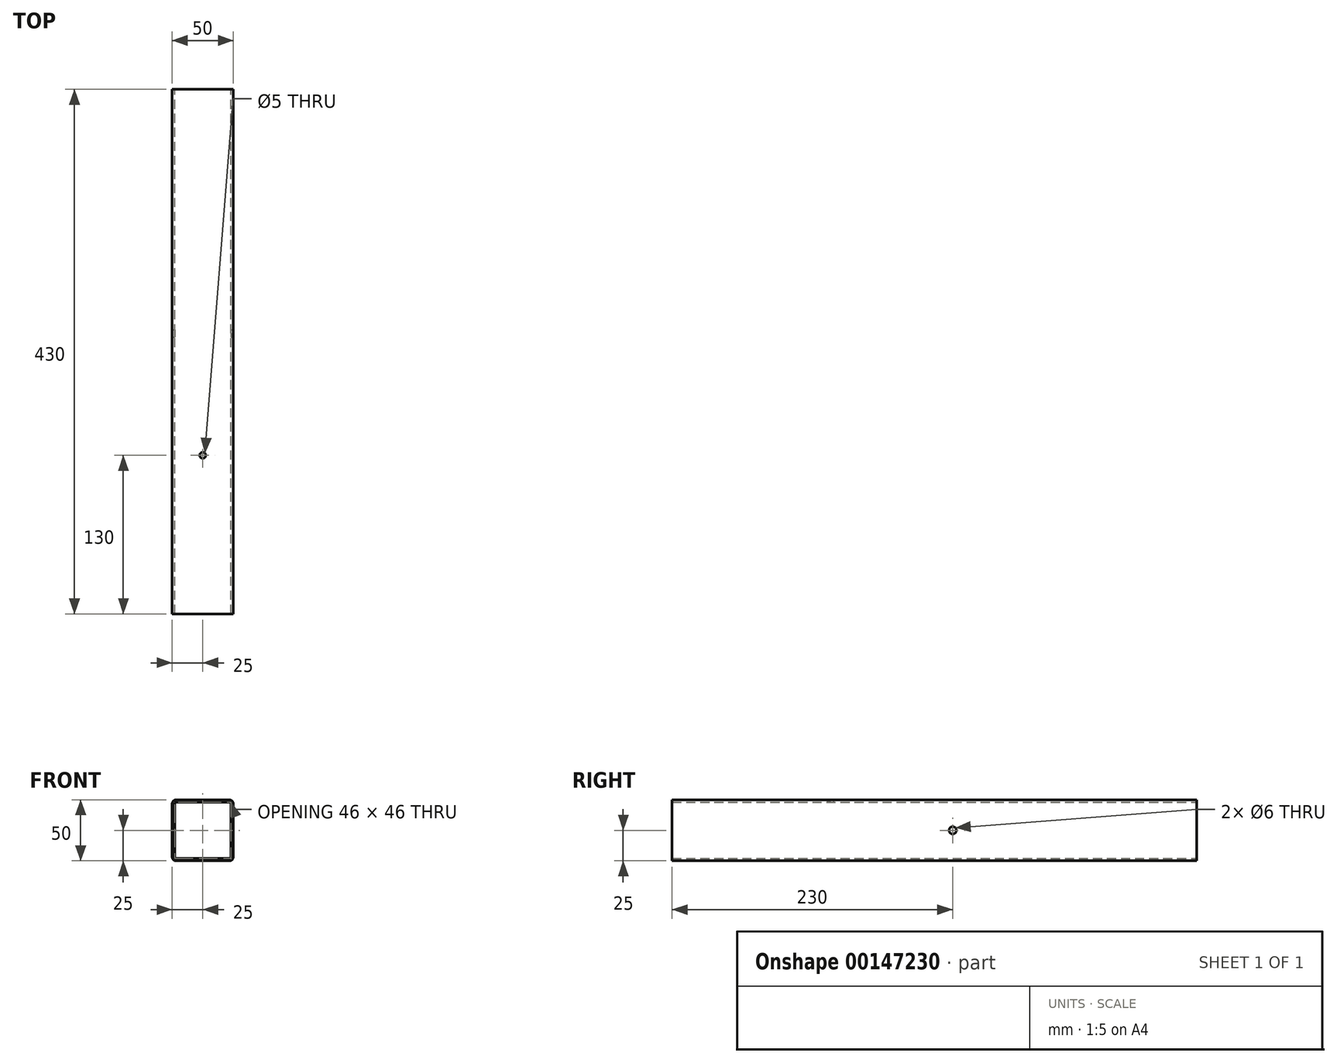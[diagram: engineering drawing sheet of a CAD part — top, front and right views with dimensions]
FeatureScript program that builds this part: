
annotation { "Feature Type Name" : "Feature", "Feature Type Description" : "" }
export const myFeature = defineFeature(function(context is Context, id is Id, definition is map)
    precondition{}
    {
        {
            var Q0;
            Q0=qCreatedBy(makeId("Front.planeOp"),FACE);
            var sketch = newSketch(context, id + "F0", { "sketchPlane" : qUnion([Q0])});
            skLineSegment(sketch, "E0.bottom", {"start": v(25, -25) * mm, "end": v(-25, -25) * mm});
            skLineSegment(sketch, "E0.top", {"start": v(25, 25) * mm, "end": v(-25, 25) * mm});
            skLineSegment(sketch, "E0.left", {"start": v(25, -25) * mm, "end": v(25, 25) * mm});
            skLineSegment(sketch, "E0.right", {"start": v(-25, -25) * mm, "end": v(-25, 25) * mm});
            skPoint(sketch, "E0.middle", {"position": v(0, 0) * mm});
            skLineSegment(sketch, "E1.0", {"start": v(23, -23) * mm, "end": v(23, 23) * mm});
            skLineSegment(sketch, "E1.1", {"start": v(23, -23) * mm, "end": v(-23, -23) * mm});
            skLineSegment(sketch, "E1.2", {"start": v(-23, -23) * mm, "end": v(-23, 23) * mm});
            skLineSegment(sketch, "E1.3", {"start": v(23, 23) * mm, "end": v(-23, 23) * mm});
            skSolve(sketch);
        }
        {
            var Q0;
            Q0 = qSketchRegion(id + "F0", true);
            extrude(context, id + "F1", {"entities" : qUnion([Q0]), "depth" : 430 * mm});
        }
        {
            var Q0;
            Q0=makeQuery(id+"F1.opExtrude","SWEPT_EDGE",EDGE,{"disambiguationData":[OSD([sQuery(id+"F0.wireOp",EDGE,"E1.2"),sQuery(id+"F0.wireOp",EDGE,"E1.3")])]});
            var Q1;
            Q1=makeQuery(id+"F1.opExtrude","SWEPT_EDGE",EDGE,{"disambiguationData":[OSD([sQuery(id+"F0.wireOp",EDGE,"E1.0"),sQuery(id+"F0.wireOp",EDGE,"E1.3")])]});
            var Q2;
            Q2=makeQuery(id+"F1.opExtrude","SWEPT_EDGE",EDGE,{"disambiguationData":[OSD([sQuery(id+"F0.wireOp",EDGE,"E1.0"),sQuery(id+"F0.wireOp",EDGE,"E1.1")])]});
            var Q3;
            Q3=makeQuery(id+"F1.opExtrude","SWEPT_EDGE",EDGE,{"disambiguationData":[OSD([sQuery(id+"F0.wireOp",EDGE,"E1.1"),sQuery(id+"F0.wireOp",EDGE,"E1.2")])]});
            fillet(context, id + "F2", {"entities" : qUnion([Q0, Q1, Q2, Q3]), "radius" : 1 * mm, "tangentPropagation" : true, "allowEdgeOverflow" : false});
        }
        {
            var Q0;
            Q0=makeQuery(id+"F1.opExtrude","SWEPT_EDGE",EDGE,{"disambiguationData":[OSD([sQuery(id+"F0.wireOp",EDGE,"E0.top"),sQuery(id+"F0.wireOp",EDGE,"E0.left")])]});
            var Q1;
            Q1=makeQuery(id+"F1.opExtrude","SWEPT_EDGE",EDGE,{"disambiguationData":[OSD([sQuery(id+"F0.wireOp",EDGE,"E0.top"),sQuery(id+"F0.wireOp",EDGE,"E0.right")])]});
            var Q2;
            Q2=makeQuery(id+"F1.opExtrude","SWEPT_EDGE",EDGE,{"disambiguationData":[OSD([sQuery(id+"F0.wireOp",EDGE,"E0.bottom"),sQuery(id+"F0.wireOp",EDGE,"E0.left")])]});
            var Q3;
            Q3=makeQuery(id+"F1.opExtrude","SWEPT_EDGE",EDGE,{"disambiguationData":[OSD([sQuery(id+"F0.wireOp",EDGE,"E0.bottom"),sQuery(id+"F0.wireOp",EDGE,"E0.right")])]});
            fillet(context, id + "F3", {"entities" : qUnion([Q0, Q1, Q2, Q3]), "radius" : 3 * mm, "tangentPropagation" : true, "allowEdgeOverflow" : false});
        }
        {
            var Q0;
            Q0=makeQuery(id+"F1.opExtrude","SWEPT_FACE",FACE,{"disambiguationData":[OSD([sQuery(id+"F0.wireOp",EDGE,"E0.top")])]});
            var sketch = newSketch(context, id + "F4", { "sketchPlane" : qUnion([Q0])});
            skCircle(sketch, "E2", {"center": v(0, -300) * mm, "radius": 2.5 * mm});
            skLineSegment(sketch, "E3", {"start": v(0, 0) * mm, "end": v(0, -300) * mm, "construction": true});
            skPoint(sketch, "E3.startSnap0", {"position": v(0, 0) * mm});
            skSolve(sketch);
        }
        {
            var Q0;
            Q0 = qSketchRegion(id + "F4", true);
            extrude(context, id + "F5", {"entities" : qUnion([Q0]), "operationType" : NewBodyOperationType.REMOVE, "oppositeDirection" : true, "depth" : 5 * mm});
        }
        {
            var Q0;
            Q0=makeQuery(id+"F1.opExtrude","SWEPT_FACE",FACE,{"disambiguationData":[OSD([sQuery(id+"F0.wireOp",EDGE,"E0.left")])]});
            var sketch = newSketch(context, id + "F6", { "sketchPlane" : qUnion([Q0])});
            skCircle(sketch, "E4", {"center": v(-200, 0) * mm, "radius": 3 * mm});
            skLineSegment(sketch, "E5", {"start": v(-200, 0) * mm, "end": v(0, 0) * mm, "construction": true});
            skSolve(sketch);
        }
        {
            var Q0;
            Q0 = qSketchRegion(id + "F6", true);
            extrude(context, id + "F7", {"entities" : qUnion([Q0]), "operationType" : NewBodyOperationType.REMOVE, "endBound" : BoundingType.THROUGH_ALL, "oppositeDirection" : true, "depth" : 25 * mm});
        }
    });
